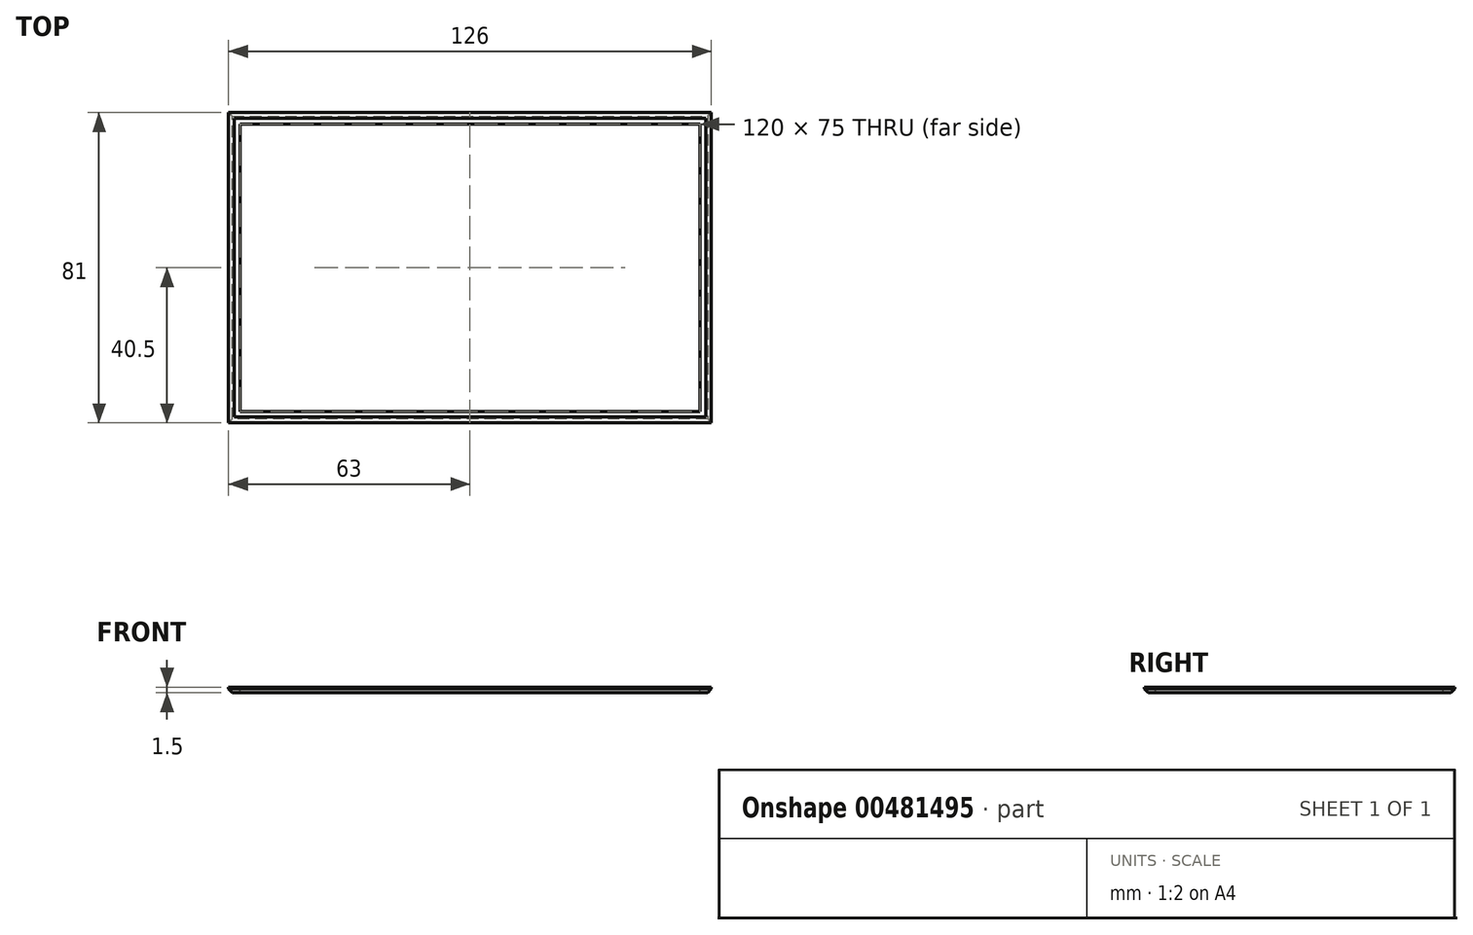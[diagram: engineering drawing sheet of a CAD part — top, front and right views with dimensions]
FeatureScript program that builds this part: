
annotation { "Feature Type Name" : "Feature", "Feature Type Description" : "" }
export const myFeature = defineFeature(function(context is Context, id is Id, definition is map)
    precondition{}
    {
        {
            var Q0;
            Q0=qCreatedBy(makeId("Top.planeOp"),FACE);
            var sketch = newSketch(context, id + "F0", { "sketchPlane" : qUnion([Q0])});
            skLineSegment(sketch, "E0.bottom", {"start": v(0, 0) * mm, "end": v(126, 0) * mm});
            skLineSegment(sketch, "E0.top", {"start": v(0, 81) * mm, "end": v(126, 81) * mm});
            skLineSegment(sketch, "E0.left", {"start": v(0, 0) * mm, "end": v(0, 81) * mm});
            skLineSegment(sketch, "E0.right", {"start": v(126, 0) * mm, "end": v(126, 81) * mm});
            skSolve(sketch);
        }
        {
            var Q0;
            Q0=makeQuery(id+"F0.imprint","IMPRINT",FACE,{"disambiguationData":[TD([[makeQuery(id+"F0.imprint","IMPRINT",EDGE,{"derivedFrom":sQuery(id+"F0.wireOp",EDGE,"E0.bottom")}),1.0]])]});
            extrude(context, id + "F1", {"entities" : qUnion([Q0]), "depth" : 1.5 * mm});
        }
        {
            var Q0;
            Q0=makeQuery(id+"F1.opExtrude","CAP_FACE",FACE,{"disambiguationData":[OSD([sQuery(id+"F0.wireOp",EDGE,"E0.bottom"),sQuery(id+"F0.wireOp",EDGE,"E0.top"),sQuery(id+"F0.wireOp",EDGE,"E0.left"),sQuery(id+"F0.wireOp",EDGE,"E0.right")])],"isStart":false});
            var sketch = newSketch(context, id + "F2", { "sketchPlane" : qUnion([Q0])});
            skLineSegment(sketch, "E1.bottom", {"start": v(3, 78) * mm, "end": v(123, 78) * mm});
            skLineSegment(sketch, "E1.top", {"start": v(3, 3) * mm, "end": v(123, 3) * mm});
            skLineSegment(sketch, "E1.left", {"start": v(3, 78) * mm, "end": v(3, 3) * mm});
            skLineSegment(sketch, "E1.right", {"start": v(123, 78) * mm, "end": v(123, 3) * mm});
            skSolve(sketch);
        }
        {
            var Q0;
            Q0=makeQuery(id+"F2.imprint","IMPRINT",FACE,{"disambiguationData":[TD([[makeQuery(id+"F2.imprint","IMPRINT",EDGE,{"derivedFrom":sQuery(id+"F2.wireOp",EDGE,"E1.bottom")}),-1.0]])]});
            extrude(context, id + "F3", {"entities" : qUnion([Q0]), "operationType" : NewBodyOperationType.REMOVE, "oppositeDirection" : true, "depth" : 25 * mm});
        }
        {
            var Q0;
            Q0=makeQuery(id+"F1.opExtrude","CAP_FACE",FACE,{"disambiguationData":[OSD([sQuery(id+"F0.wireOp",EDGE,"E0.bottom"),sQuery(id+"F0.wireOp",EDGE,"E0.top"),sQuery(id+"F0.wireOp",EDGE,"E0.left"),sQuery(id+"F0.wireOp",EDGE,"E0.right")])],"isStart":false});
            var sketch = newSketch(context, id + "F4", { "sketchPlane" : qUnion([Q0])});
            skLineSegment(sketch, "E2.bottom", {"start": v(1.5, 79.5) * mm, "end": v(124.5, 79.5) * mm});
            skLineSegment(sketch, "E2.top", {"start": v(1.5, 1.5) * mm, "end": v(124.5, 1.5) * mm});
            skLineSegment(sketch, "E2.left", {"start": v(1.5, 79.5) * mm, "end": v(1.5, 1.5) * mm});
            skLineSegment(sketch, "E2.right", {"start": v(124.5, 79.5) * mm, "end": v(124.5, 1.5) * mm});
            skSolve(sketch);
        }
        {
            var Q0;
            Q0 = qSketchRegion(id + "F4", true);
            extrude(context, id + "F5", {"entities" : qUnion([Q0]), "operationType" : NewBodyOperationType.REMOVE, "oppositeDirection" : true, "depth" : 0.4 * mm});
        }
        {
            var Q0;
            Q0=makeQuery(id+"F1.opExtrude","CAP_EDGE",EDGE,{"disambiguationData":[OSD([sQuery(id+"F0.wireOp",EDGE,"E0.right")])],"isStart":true});
            var Q1;
            Q1=makeQuery(id+"F1.opExtrude","CAP_EDGE",EDGE,{"disambiguationData":[OSD([sQuery(id+"F0.wireOp",EDGE,"E0.top")])],"isStart":true});
            var Q2;
            Q2=makeQuery(id+"F1.opExtrude","CAP_EDGE",EDGE,{"disambiguationData":[OSD([sQuery(id+"F0.wireOp",EDGE,"E0.left")])],"isStart":true});
            var Q3;
            Q3=makeQuery(id+"F1.opExtrude","CAP_EDGE",EDGE,{"disambiguationData":[OSD([sQuery(id+"F0.wireOp",EDGE,"E0.bottom")])],"isStart":true});
            chamfer(context, id + "F6", {"entities" : qUnion([Q0, Q1, Q2, Q3]), "width" : 1 * mm, "tangentPropagation" : true});
        }
    });
